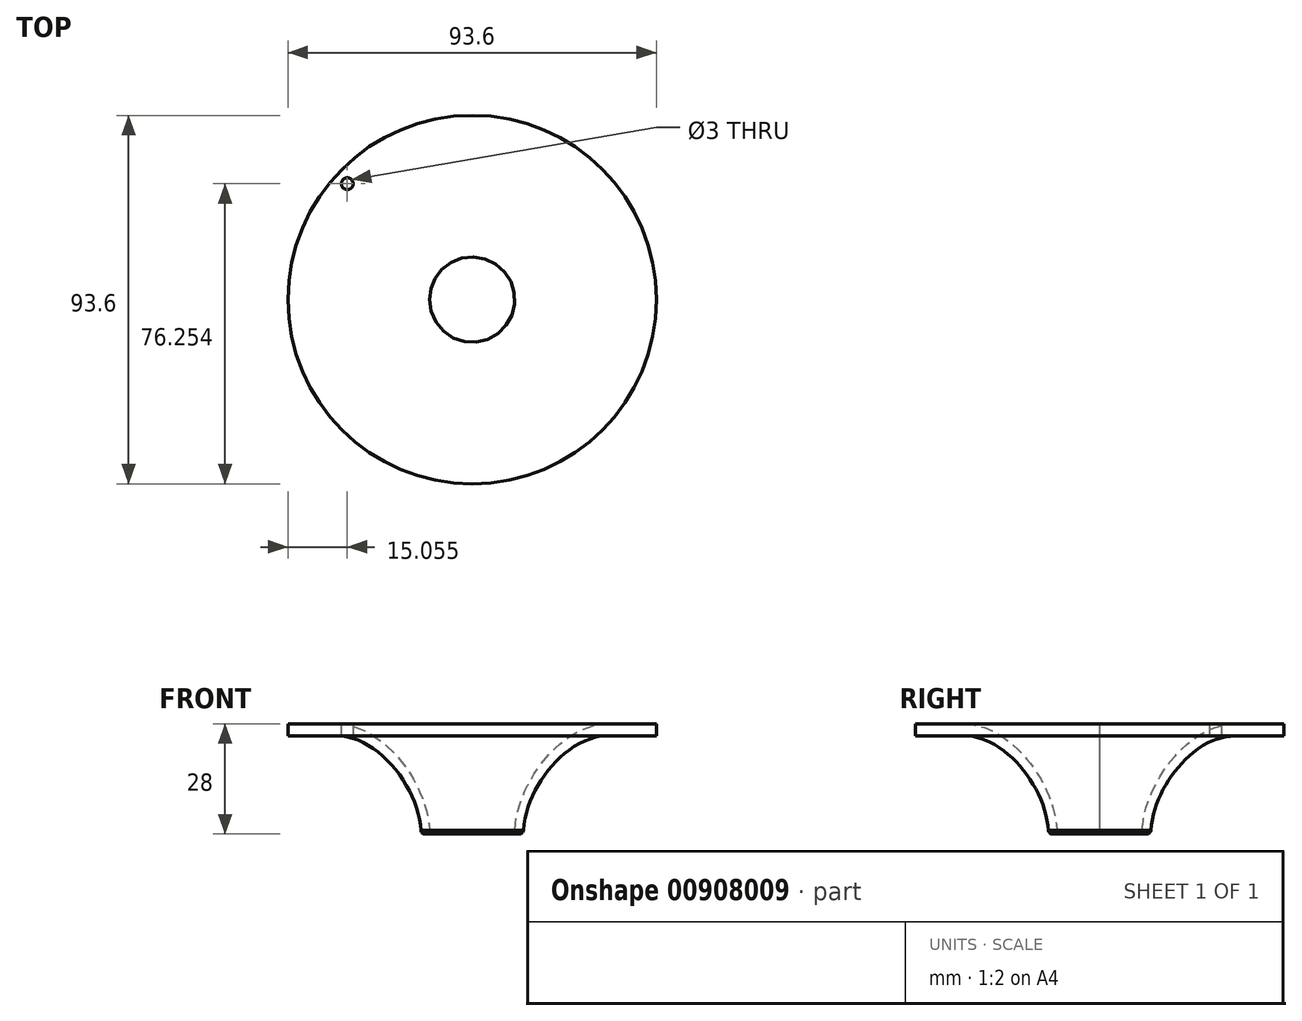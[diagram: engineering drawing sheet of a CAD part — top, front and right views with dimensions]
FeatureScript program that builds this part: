
annotation { "Feature Type Name" : "Feature", "Feature Type Description" : "" }
export const myFeature = defineFeature(function(context is Context, id is Id, definition is map)
    precondition{}
    {
        {
            var Q0;
            Q0=qCreatedBy(makeId("Front.planeOp"),FACE);
            var sketch = newSketch(context, id + "F0", { "sketchPlane" : qUnion([Q0])});
            skLineSegment(sketch, "E0", {"start": v(-46.8, 28) * mm, "end": v(-46.8, 25) * mm});
            skLineSegment(sketch, "E1", {"start": v(-46.8, 28) * mm, "end": v(-34.48, 28) * mm});
            skLineSegment(sketch, "E2", {"start": v(-46.8, 25) * mm, "end": v(-34.48, 25) * mm});
            skLineSegment(sketch, "E3", {"start": v(-10.8, 0) * mm, "end": v(-12.98, 0) * mm});
            skFitSpline(sketch, "E4", {"points": [v(-34.48, 25) * mm, v(-12.98, 0) * mm], "startDerivative": vector(32.73, 0) * mm, "endDerivative": vector(0, -32.73) * mm});
            skLineSegment(sketch, "E5", {"start": v(-12.98, 0) * mm, "end": v(-12.98, -26.95) * mm, "construction": true});
            skLineSegment(sketch, "E6", {"start": v(-10.8, 0) * mm, "end": v(-10.8, -26.82) * mm, "construction": true});
            skFitSpline(sketch, "E7", {"points": [v(-34.48, 28) * mm, v(-10.8, 0) * mm], "startDerivative": vector(36.43, 0) * mm, "endDerivative": vector(0, -36.43) * mm});
            skLineSegment(sketch, "E8", {"start": v(0, 0) * mm, "end": v(0, 51.48) * mm, "construction": true});
            skSolve(sketch);
        }
        {
            var Q0;
            Q0=makeQuery(id+"F0.imprint","IMPRINT",FACE,{"disambiguationData":[TD([[makeQuery(id+"F0.imprint","IMPRINT",EDGE,{"derivedFrom":sQuery(id+"F0.wireOp",EDGE,"E0")}),1.0]])]});
            var Q1;
            Q1=sQuery(id+"F0.wireOp",EDGE,"E8");
            revolve(context, id + "F1", {"surfaceOperationType" : NewSurfaceOperationType.NEW, "entities" : qUnion([Q0]), "axis" : qUnion([Q1]), "revolveType" : RevolveType.FULL});
        }
        {
            var Q0;
            Q0=qCreatedBy(makeId("Top.planeOp"),FACE);
            var sketch = newSketch(context, id + "F2", { "sketchPlane" : qUnion([Q0])});
            skPoint(sketch, "E9", {"position": v(-31.75, 29.45) * mm});
            skLineSegment(sketch, "E10", {"start": v(0, 0) * mm, "end": v(50.7, 0) * mm, "construction": true});
            skLineSegment(sketch, "E11", {"start": v(0, 0) * mm, "end": v(0, -60.18) * mm, "construction": true});
            skSolve(sketch);
        }
        {
            var Q0;
            Q0=sQuery(id+"F2.wireOp",VERTEX,"E9");
            var Q1;
            Q1=makeQuery(id+"F1.opRevolve","SWEPT_BODY",BODY,{"disambiguationData":[OSD([sQuery(id+"F0.wireOp",EDGE,"E0"),sQuery(id+"F0.wireOp",EDGE,"E1"),sQuery(id+"F0.wireOp",EDGE,"E2"),sQuery(id+"F0.wireOp",EDGE,"E3"),sQuery(id+"F0.wireOp",EDGE,"E4"),sQuery(id+"F0.wireOp",EDGE,"E7")])]});
            hole(context, id + "F3", {"style" : HoleStyle.SIMPLE, "endStyle" : HoleEndStyle.THROUGH, "oppositeDirection" : true, "holeDiameter" : 3 * mm, "majorDiameter" : 5 * mm, "isTappedThrough" : true, "tappedDepth" : 12 * mm, "tapClearance" : 3, "locations" : qUnion([Q0]), "scope" : qUnion([Q1])});
        }
        {
            var Q0;
            Q0=qCreatedBy(makeId("Right.planeOp"),FACE);
            var sketch = newSketch(context, id + "F4", { "sketchPlane" : qUnion([Q0])});
            skLineSegment(sketch, "E12", {"start": v(0, 0) * mm, "end": v(0, 55.6) * mm, "construction": true});
            skSolve(sketch);
        }
        {
            var Q0;
            Q0=makeQuery(id+"F1.opRevolve","SWEPT_EDGE",EDGE,{"disambiguationData":[OSD([sQuery(id+"F0.wireOp",EDGE,"E3"),sQuery(id+"F0.wireOp",EDGE,"E4")])]});
            var Q1;
            Q1=makeQuery(id+"F1.opRevolve","SWEPT_EDGE",EDGE,{"disambiguationData":[OSD([sQuery(id+"F0.wireOp",EDGE,"E3"),sQuery(id+"F0.wireOp",EDGE,"E7")])]});
            fillet(context, id + "F5", {"entities" : qUnion([Q0, Q1]), "radius" : 1 * mm, "tangentPropagation" : true, "allowEdgeOverflow" : false});
        }
    });
